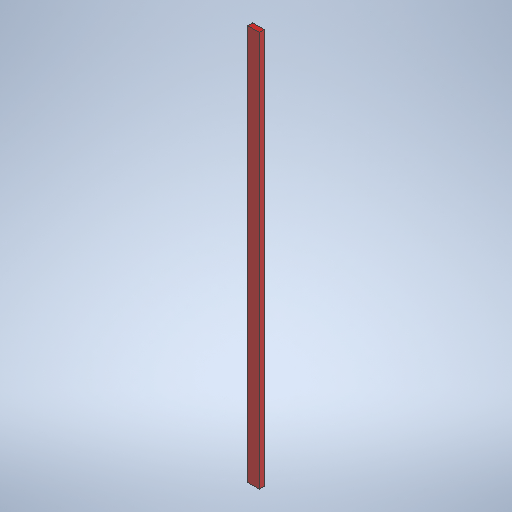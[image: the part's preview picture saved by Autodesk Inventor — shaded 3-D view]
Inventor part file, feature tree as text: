
AUTODESK INVENTOR PART (.ipt)
format: ipt  version: 2025.1 (Build 291241020, 241B)  size: 257,536 bytes
history: native  units: in
note: dims shown in document units (in); Inventor stores cm internally (conversion verified against a paired STEP export)
features: extrude x1, sketch x1, other x1
ambient origin geometry x8: Origin, YZ Plane, XZ Plane, XY Plane, X Axis, Y Axis, Z Axis, Center Point
bodies: Solid1 (feature_tree)
feature tree (3):
  extrude  "Extrusion1"  Depth=3.5in
  sketch  "Sketch1"  dims[d0=1.5in d1=3.5in d2=120.0in d3=0.0in]
  other  "Finish1"
